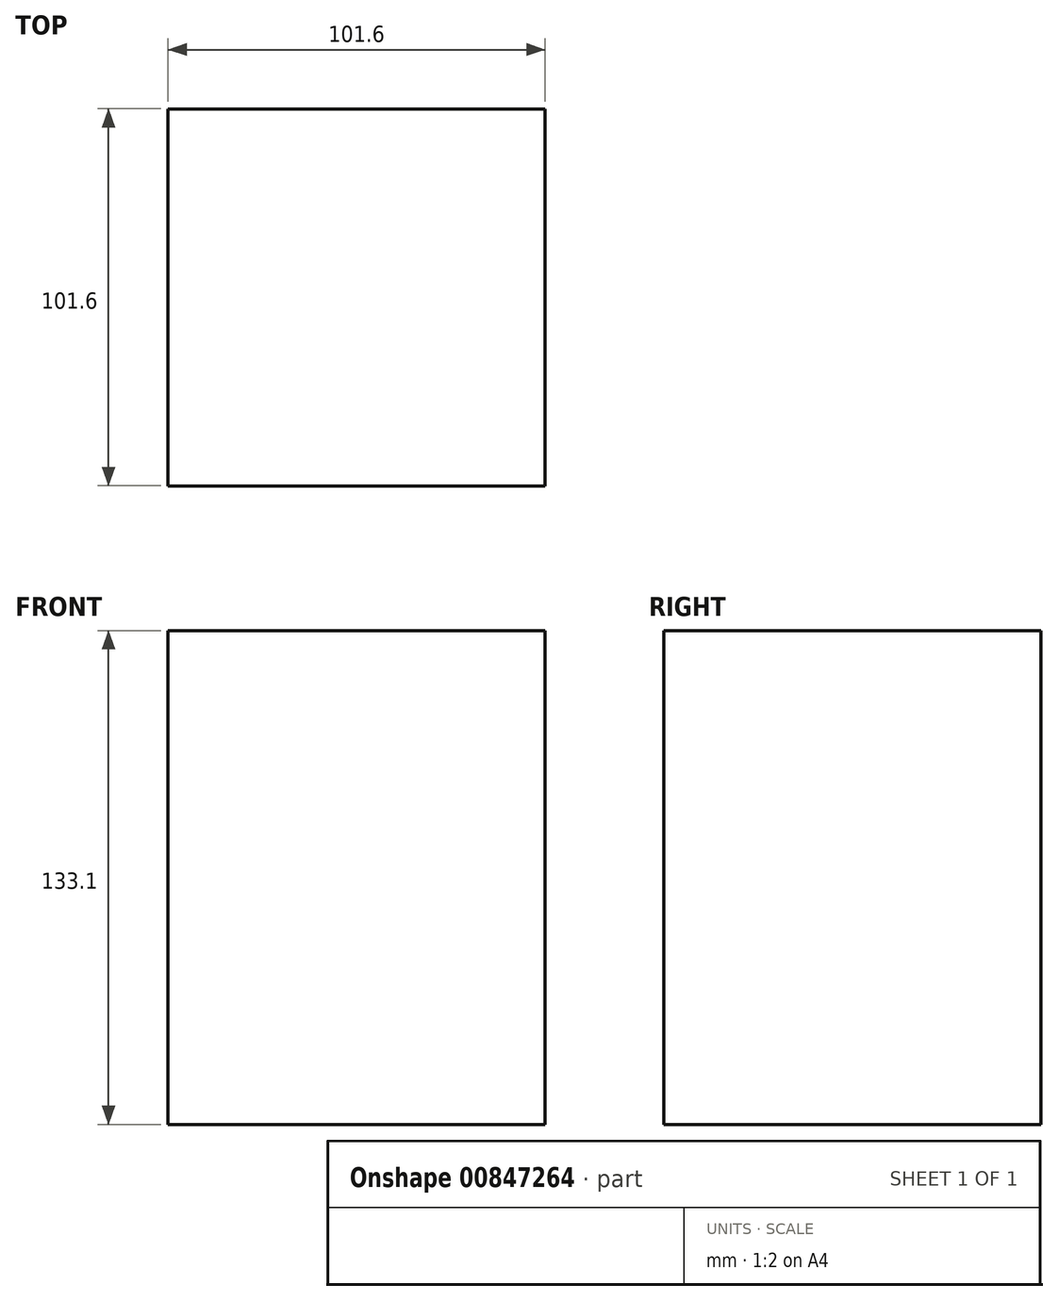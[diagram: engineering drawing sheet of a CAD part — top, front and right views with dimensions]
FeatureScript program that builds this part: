
annotation { "Feature Type Name" : "Feature", "Feature Type Description" : "" }
export const myFeature = defineFeature(function(context is Context, id is Id, definition is map)
    precondition{}
    {
        {
            var Q0;
            Q0=qCreatedBy(makeId("Top.planeOp"),FACE);
            var sketch = newSketch(context, id + "F0", { "sketchPlane" : qUnion([Q0])});
            skLineSegment(sketch, "E0.bottom", {"start": v(-50.07, 54.97) * mm, "end": v(51.53, 54.97) * mm});
            skLineSegment(sketch, "E0.top", {"start": v(-50.07, -46.63) * mm, "end": v(51.53, -46.63) * mm});
            skLineSegment(sketch, "E0.left", {"start": v(-50.07, 54.97) * mm, "end": v(-50.07, -46.63) * mm});
            skLineSegment(sketch, "E0.right", {"start": v(51.53, 54.97) * mm, "end": v(51.53, -46.63) * mm});
            skSolve(sketch);
        }
        {
            var Q0;
            Q0=makeQuery(id+"F0.imprint","IMPRINT",FACE,{"disambiguationData":[TD([[makeQuery(id+"F0.imprint","IMPRINT",EDGE,{"derivedFrom":sQuery(id+"F0.wireOp",EDGE,"E0.bottom")}),-1.0]])]});
            extrude(context, id + "F1", {"entities" : qUnion([Q0]), "depth" : 133.1 * mm, "offsetDistance" : 25.4 * mm});
        }
    });
